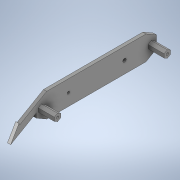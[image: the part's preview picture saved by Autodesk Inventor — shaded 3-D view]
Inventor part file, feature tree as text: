
AUTODESK INVENTOR PART (.ipt)
format: ipt  version: 2020 (Build 240168000, 168)  size: 166,912 bytes
history: native  units: in
note: dims shown in document units (in); Inventor stores cm internally (conversion verified against a paired STEP export)
features: other x3, extrude x1, sketch x1
ambient origin geometry x8: Origin, YZ Plane, XZ Plane, XY Plane, X Axis, Y Axis, Z Axis, Center Point
bodies: Solid1 (feature_tree)
feature tree (5):
  other  "HexWheelGuard.ipt"
  extrude  "Extrusion1"  TaperAngle=0.0deg  [1 undecoded]
  other  "Solid1::HexWheelGuard.ipt"
  other  "TaggingFeature1"
  sketch  "Sketch1"  dims[d0=0.3937in d6=0.0in d7=0.0in d9=0.315in d10=1.3858in d11=60.0deg d12=0.0787in]
note: 1 required parameter value undecoded (feature->parameter linkage not recoverable at this tier; creation-order binding heuristic only, values carry confidence <= 0.55)
